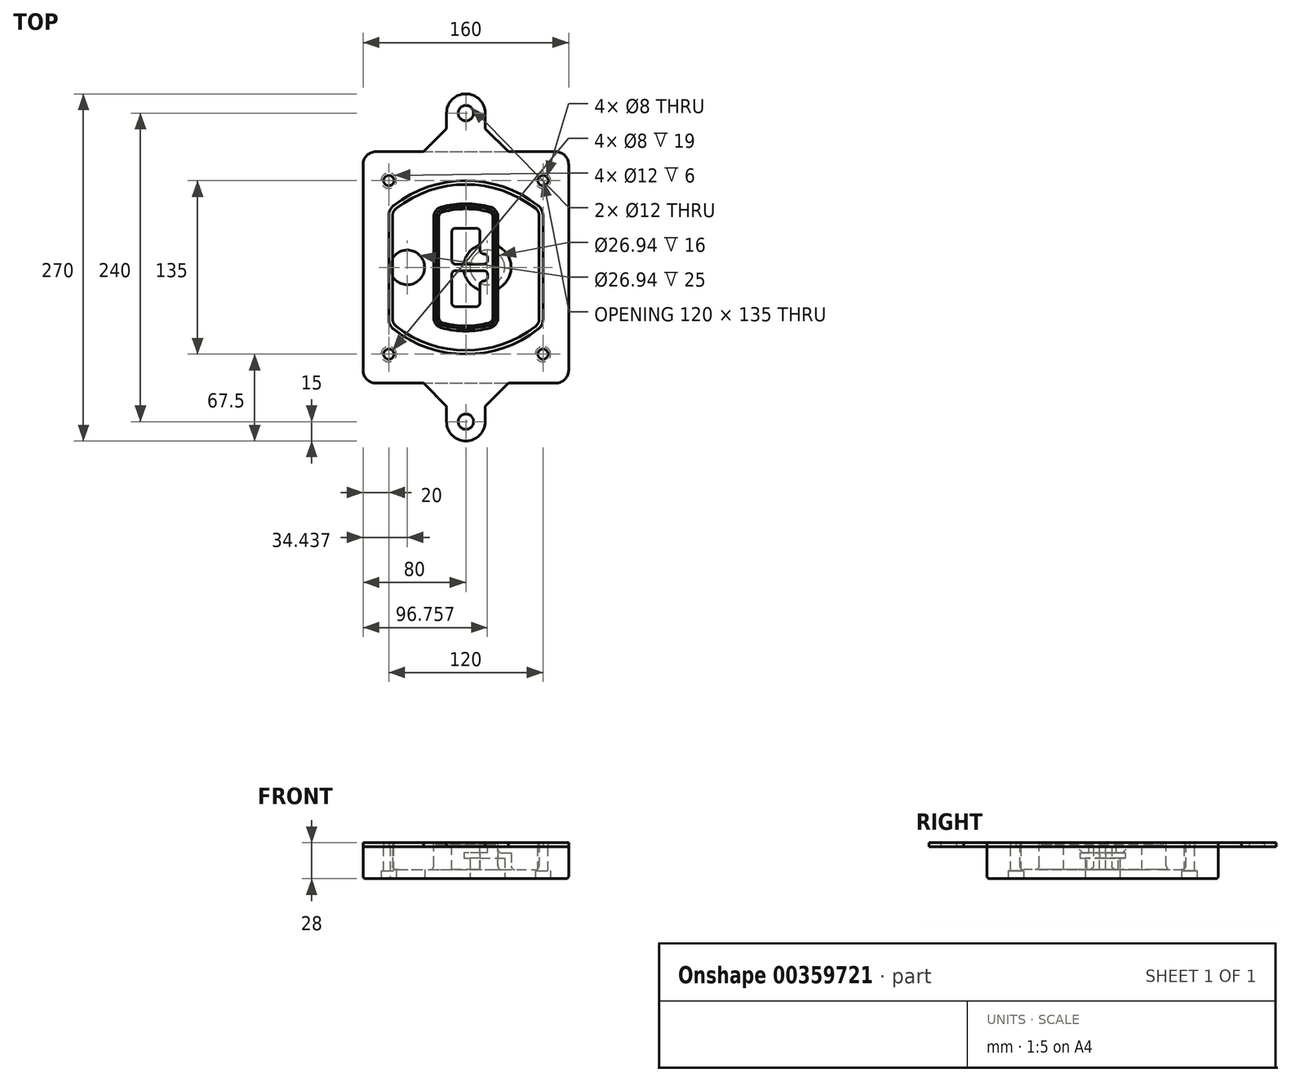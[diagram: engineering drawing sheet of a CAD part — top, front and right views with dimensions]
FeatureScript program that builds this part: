
annotation { "Feature Type Name" : "Feature", "Feature Type Description" : "" }
export const myFeature = defineFeature(function(context is Context, id is Id, definition is map)
    precondition{}
    {
        {
            var Q0;
            Q0=qCreatedBy(makeId("Top.planeOp"),FACE);
            var sketch = newSketch(context, id + "F0", { "sketchPlane" : qUnion([Q0])});
            skPoint(sketch, "E0.rect.middle", {"position": v(0, 0) * mm});
            skLineSegment(sketch, "E1.bottom", {"start": v(-70, -90) * mm, "end": v(70, -90) * mm});
            skLineSegment(sketch, "E1.top", {"start": v(-70, 90) * mm, "end": v(70, 90) * mm});
            skLineSegment(sketch, "E1.left", {"start": v(-80, -80) * mm, "end": v(-80, 80) * mm});
            skLineSegment(sketch, "E1.right", {"start": v(80, -80) * mm, "end": v(80, 80) * mm});
            skLineSegment(sketch, "E2", {"start": v(-80, 90) * mm, "end": v(80, -90) * mm, "construction": true});
            skLineSegment(sketch, "E3", {"start": v(80, 90) * mm, "end": v(-80, -90) * mm, "construction": true});
            skCircle(sketch, "E4", {"center": v(-60, 67.5) * mm, "radius": 4 * mm});
            skCircle(sketch, "E5", {"center": v(60, 67.5) * mm, "radius": 4 * mm});
            skCircle(sketch, "E6", {"center": v(60, -67.5) * mm, "radius": 4 * mm});
            skCircle(sketch, "E7", {"center": v(-60, -67.5) * mm, "radius": 4 * mm});
            skLineSegment(sketch, "E8", {"start": v(-60, 67.5) * mm, "end": v(60, 67.5) * mm, "construction": true});
            skLineSegment(sketch, "E9", {"start": v(60, 67.5) * mm, "end": v(60, -67.5) * mm, "construction": true});
            skLineSegment(sketch, "E10", {"start": v(60, -67.5) * mm, "end": v(-60, -67.5) * mm, "construction": true});
            skLineSegment(sketch, "E11", {"start": v(-60, -67.5) * mm, "end": v(-60, 67.5) * mm, "construction": true});
            skLineSegment(sketch, "E12", {"start": v(-60, 40.3) * mm, "end": v(-60, -40.3) * mm});
            skLineSegment(sketch, "E13", {"start": v(60, 40.3) * mm, "end": v(60, -40.3) * mm});
            skArc(sketch, "E14", {"start": v(56.15, 48.18) * mm, "mid": v(0, 67.5) * mm, "end": v(-56.15, 48.18) * mm});
            skArc(sketch, "E15", {"start": v(-56.15, -48.18) * mm, "mid": v(0, -67.5) * mm, "end": v(56.15, -48.18) * mm});
            skLineSegment(sketch, "E16", {"start": v(-60, 0) * mm, "end": v(60, 0) * mm, "construction": true});
            skPoint(sketch, "E17.visualSharp", {"position": v(-60, -45) * mm});
            skArc(sketch, "E17.filletArc", {"start": v(-60, -40.3) * mm, "mid": v(-58.99, -44.68) * mm, "end": v(-56.15, -48.18) * mm});
            skPoint(sketch, "E18.visualSharp", {"position": v(-60, 45) * mm});
            skArc(sketch, "E18.filletArc", {"start": v(-56.15, 48.18) * mm, "mid": v(-58.99, 44.68) * mm, "end": v(-60, 40.3) * mm});
            skPoint(sketch, "E19.visualSharp", {"position": v(60, 45) * mm});
            skArc(sketch, "E19.filletArc", {"start": v(60, 40.3) * mm, "mid": v(58.99, 44.68) * mm, "end": v(56.15, 48.18) * mm});
            skPoint(sketch, "E20.visualSharp", {"position": v(60, -45) * mm});
            skArc(sketch, "E20.filletArc", {"start": v(56.15, -48.18) * mm, "mid": v(58.99, -44.68) * mm, "end": v(60, -40.3) * mm});
            skPoint(sketch, "E21.visualSharp", {"position": v(-80, 90) * mm});
            skArc(sketch, "E21.filletArc", {"start": v(-70, 90) * mm, "mid": v(-77.07, 87.07) * mm, "end": v(-80, 80) * mm});
            skPoint(sketch, "E22.visualSharp", {"position": v(80, 90) * mm});
            skArc(sketch, "E22.filletArc", {"start": v(80, 80) * mm, "mid": v(77.07, 87.07) * mm, "end": v(70, 90) * mm});
            skPoint(sketch, "E23.visualSharp", {"position": v(80, -90) * mm});
            skArc(sketch, "E23.filletArc", {"start": v(70, -90) * mm, "mid": v(77.07, -87.07) * mm, "end": v(80, -80) * mm});
            skPoint(sketch, "E24.visualSharp", {"position": v(-80, -90) * mm});
            skArc(sketch, "E24.filletArc", {"start": v(-80, -80) * mm, "mid": v(-77.07, -87.07) * mm, "end": v(-70, -90) * mm});
            skArc(sketch, "E25.0", {"start": v(57, 40.3) * mm, "mid": v(56.3, 43.36) * mm, "end": v(54.3, 45.81) * mm});
            skLineSegment(sketch, "E25.1", {"start": v(57, 40.3) * mm, "end": v(57, -40.3) * mm});
            skArc(sketch, "E25.2", {"start": v(54.3, -45.81) * mm, "mid": v(56.3, -43.36) * mm, "end": v(57, -40.3) * mm});
            skArc(sketch, "E25.3", {"start": v(-54.3, -45.81) * mm, "mid": v(0, -64.5) * mm, "end": v(54.3, -45.81) * mm});
            skArc(sketch, "E25.4", {"start": v(-57, -40.3) * mm, "mid": v(-56.3, -43.36) * mm, "end": v(-54.3, -45.81) * mm});
            skArc(sketch, "E25.5", {"start": v(54.3, 45.81) * mm, "mid": v(0, 64.5) * mm, "end": v(-54.3, 45.81) * mm});
            skLineSegment(sketch, "E25.6", {"start": v(-57, 40.3) * mm, "end": v(-57, -40.3) * mm});
            skArc(sketch, "E25.7", {"start": v(-54.3, 45.81) * mm, "mid": v(-56.3, 43.36) * mm, "end": v(-57, 40.3) * mm});
            skArc(sketch, "E26.0", {"start": v(-58.62, 51.33) * mm, "mid": v(-62.58, 46.43) * mm, "end": v(-64, 40.3) * mm});
            skArc(sketch, "E26.1", {"start": v(58.62, 51.33) * mm, "mid": v(0, 71.5) * mm, "end": v(-58.62, 51.33) * mm});
            skArc(sketch, "E26.2", {"start": v(64, 40.3) * mm, "mid": v(62.58, 46.43) * mm, "end": v(58.62, 51.33) * mm});
            skLineSegment(sketch, "E26.3", {"start": v(64, 40.3) * mm, "end": v(64, -40.3) * mm});
            skArc(sketch, "E26.4", {"start": v(58.62, -51.33) * mm, "mid": v(62.58, -46.43) * mm, "end": v(64, -40.3) * mm});
            skLineSegment(sketch, "E26.5", {"start": v(-64, 40.3) * mm, "end": v(-64, -40.3) * mm});
            skArc(sketch, "E26.6", {"start": v(-58.62, -51.33) * mm, "mid": v(0, -71.5) * mm, "end": v(58.62, -51.33) * mm});
            skArc(sketch, "E26.7", {"start": v(-64, -40.3) * mm, "mid": v(-62.58, -46.43) * mm, "end": v(-58.62, -51.33) * mm});
            skSolve(sketch);
        }
        {
            var Q0;
            Q0=makeQuery(id+"F0.imprint","IMPRINT",FACE,{"disambiguationData":[TD([[makeQuery(id+"F0.imprint","IMPRINT",EDGE,{"derivedFrom":sQuery(id+"F0.wireOp",EDGE,"E1.bottom")}),1.0]])]});
            var Q1;
            Q1=makeQuery(id+"F0.imprint","IMPRINT",FACE,{"disambiguationData":[TD([[makeQuery(id+"F0.imprint","IMPRINT",EDGE,{"derivedFrom":sQuery(id+"F0.wireOp",EDGE,"E12")}),1.0]])]});
            var Q2;
            Q2=makeQuery(id+"F0.imprint","IMPRINT",FACE,{"disambiguationData":[TD([[makeQuery(id+"F0.imprint","IMPRINT",EDGE,{"derivedFrom":sQuery(id+"F0.wireOp",EDGE,"E25.0")}),1.0]])]});
            var Q3;
            Q3=makeQuery(id+"F0.imprint","IMPRINT",FACE,{"disambiguationData":[TD([[makeQuery(id+"F0.imprint","IMPRINT",EDGE,{"derivedFrom":sQuery(id+"F0.wireOp",EDGE,"E12")}),-1.0]])]});
            extrude(context, id + "F1", {"entities" : qUnion([Q0, Q1, Q2, Q3]), "oppositeDirection" : true, "depth" : 25 * mm});
        }
        {
            var Q0;
            Q0=makeQuery(id+"F0.imprint","IMPRINT",FACE,{"disambiguationData":[TD([[makeQuery(id+"F0.imprint","IMPRINT",EDGE,{"derivedFrom":sQuery(id+"F0.wireOp",EDGE,"E12")}),1.0]])]});
            extrude(context, id + "F2", {"entities" : qUnion([Q0]), "operationType" : NewBodyOperationType.ADD, "depth" : 3 * mm});
        }
        {
            var Q0;
            Q0=makeQuery(id+"F0.imprint","IMPRINT",FACE,{"disambiguationData":[TD([[makeQuery(id+"F0.imprint","IMPRINT",EDGE,{"derivedFrom":sQuery(id+"F0.wireOp",EDGE,"E25.0")}),1.0]])]});
            extrude(context, id + "F3", {"entities" : qUnion([Q0]), "operationType" : NewBodyOperationType.REMOVE, "oppositeDirection" : true, "depth" : 18 * mm});
        }
        {
            var Q0;
            Q0=makeQuery(id+"F2.opExtrude","CAP_FACE",FACE,{"disambiguationData":[OSD([sQuery(id+"F0.wireOp",EDGE,"E12"),sQuery(id+"F0.wireOp",EDGE,"E13"),sQuery(id+"F0.wireOp",EDGE,"E14"),sQuery(id+"F0.wireOp",EDGE,"E15"),sQuery(id+"F0.wireOp",EDGE,"E17.filletArc"),sQuery(id+"F0.wireOp",EDGE,"E18.filletArc"),sQuery(id+"F0.wireOp",EDGE,"E19.filletArc"),sQuery(id+"F0.wireOp",EDGE,"E20.filletArc"),sQuery(id+"F0.wireOp",EDGE,"E25.0"),sQuery(id+"F0.wireOp",EDGE,"E25.1"),sQuery(id+"F0.wireOp",EDGE,"E25.2"),sQuery(id+"F0.wireOp",EDGE,"E25.3"),sQuery(id+"F0.wireOp",EDGE,"E25.4"),sQuery(id+"F0.wireOp",EDGE,"E25.5"),sQuery(id+"F0.wireOp",EDGE,"E25.6"),sQuery(id+"F0.wireOp",EDGE,"E25.7")])],"isStart":false});
            var sketch = newSketch(context, id + "F4", { "sketchPlane" : qUnion([Q0])});
            skArc(sketch, "E27.0", {"start": v(-19.08, -46.97) * mm, "mid": v(0, -49.5) * mm, "end": v(19.08, -46.97) * mm});
            skArc(sketch, "E28.0", {"start": v(19.08, 46.97) * mm, "mid": v(0, 49.5) * mm, "end": v(-19.08, 46.97) * mm});
            skLineSegment(sketch, "E29", {"start": v(-25, 39.25) * mm, "end": v(-25, -39.25) * mm});
            skLineSegment(sketch, "E30", {"start": v(25, 39.25) * mm, "end": v(25, -39.25) * mm});
            skLineSegment(sketch, "E31", {"start": v(-25, 45.1) * mm, "end": v(25, 45.1) * mm, "construction": true});
            skLineSegment(sketch, "E32", {"start": v(-25, -45.1) * mm, "end": v(25, -45.1) * mm, "construction": true});
            skPoint(sketch, "E33.visualSharp", {"position": v(-25, 45.1) * mm});
            skArc(sketch, "E33.filletArc", {"start": v(-19.08, 46.97) * mm, "mid": v(-23.35, 44.11) * mm, "end": v(-25, 39.25) * mm});
            skPoint(sketch, "E34.visualSharp", {"position": v(25, 45.1) * mm});
            skArc(sketch, "E34.filletArc", {"start": v(25, 39.25) * mm, "mid": v(23.35, 44.11) * mm, "end": v(19.08, 46.97) * mm});
            skPoint(sketch, "E35.visualSharp", {"position": v(25, -45.1) * mm});
            skArc(sketch, "E35.filletArc", {"start": v(19.08, -46.97) * mm, "mid": v(23.35, -44.11) * mm, "end": v(25, -39.25) * mm});
            skPoint(sketch, "E36.visualSharp", {"position": v(-25, -45.1) * mm});
            skArc(sketch, "E36.filletArc", {"start": v(-25, -39.25) * mm, "mid": v(-23.35, -44.11) * mm, "end": v(-19.08, -46.97) * mm});
            skArc(sketch, "E37.0", {"start": v(54.3, 45.81) * mm, "mid": v(0, 64.5) * mm, "end": v(-54.3, 45.81) * mm});
            skArc(sketch, "E37.1", {"start": v(-54.3, 45.81) * mm, "mid": v(-56.3, 43.36) * mm, "end": v(-57, 40.3) * mm});
            skLineSegment(sketch, "E37.2", {"start": v(-57, 40.3) * mm, "end": v(-57, -40.3) * mm});
            skArc(sketch, "E37.3", {"start": v(-57, -40.3) * mm, "mid": v(-56.3, -43.36) * mm, "end": v(-54.3, -45.81) * mm});
            skArc(sketch, "E37.4", {"start": v(-54.3, -45.81) * mm, "mid": v(0, -64.5) * mm, "end": v(54.3, -45.81) * mm});
            skArc(sketch, "E37.5", {"start": v(54.3, -45.81) * mm, "mid": v(56.3, -43.36) * mm, "end": v(57, -40.3) * mm});
            skLineSegment(sketch, "E37.6", {"start": v(57, 40.3) * mm, "end": v(57, -40.3) * mm});
            skArc(sketch, "E37.7", {"start": v(57, 40.3) * mm, "mid": v(56.3, 43.36) * mm, "end": v(54.3, 45.81) * mm});
            skLineSegment(sketch, "E38.0", {"start": v(23, 39.25) * mm, "end": v(23, -39.25) * mm});
            skArc(sketch, "E38.1", {"start": v(18.56, -45.04) * mm, "mid": v(21.76, -42.9) * mm, "end": v(23, -39.25) * mm});
            skArc(sketch, "E38.2", {"start": v(-18.56, -45.04) * mm, "mid": v(0, -47.5) * mm, "end": v(18.56, -45.04) * mm});
            skArc(sketch, "E38.3", {"start": v(-23, -39.25) * mm, "mid": v(-21.76, -42.9) * mm, "end": v(-18.56, -45.04) * mm});
            skLineSegment(sketch, "E38.4", {"start": v(-23, 39.25) * mm, "end": v(-23, -39.25) * mm});
            skArc(sketch, "E38.5", {"start": v(23, 39.25) * mm, "mid": v(21.76, 42.9) * mm, "end": v(18.56, 45.04) * mm});
            skArc(sketch, "E38.6", {"start": v(-18.56, 45.04) * mm, "mid": v(-21.76, 42.9) * mm, "end": v(-23, 39.25) * mm});
            skArc(sketch, "E38.7", {"start": v(18.56, 45.04) * mm, "mid": v(0, 47.5) * mm, "end": v(-18.56, 45.04) * mm});
            skArc(sketch, "E39.0", {"start": v(21, 39.25) * mm, "mid": v(20.18, 41.68) * mm, "end": v(18.04, 43.1) * mm});
            skLineSegment(sketch, "E39.1", {"start": v(21, 39.25) * mm, "end": v(21, -39.25) * mm});
            skArc(sketch, "E39.2", {"start": v(18.04, -43.1) * mm, "mid": v(20.18, -41.68) * mm, "end": v(21, -39.25) * mm});
            skArc(sketch, "E39.3", {"start": v(-18.04, -43.1) * mm, "mid": v(0, -45.5) * mm, "end": v(18.04, -43.1) * mm});
            skArc(sketch, "E39.4", {"start": v(-21, -39.25) * mm, "mid": v(-20.18, -41.68) * mm, "end": v(-18.04, -43.1) * mm});
            skArc(sketch, "E39.5", {"start": v(18.04, 43.1) * mm, "mid": v(0, 45.5) * mm, "end": v(-18.04, 43.1) * mm});
            skLineSegment(sketch, "E39.6", {"start": v(-21, 39.25) * mm, "end": v(-21, -39.25) * mm});
            skArc(sketch, "E39.7", {"start": v(-18.04, 43.1) * mm, "mid": v(-20.18, 41.68) * mm, "end": v(-21, 39.25) * mm});
            skLineSegment(sketch, "E40", {"start": v(-25, 0) * mm, "end": v(25, 0) * mm, "construction": true});
            skLineSegment(sketch, "E41", {"start": v(-11, 5.5) * mm, "end": v(-11, 27.5) * mm});
            skLineSegment(sketch, "E42", {"start": v(-8, 30.5) * mm, "end": v(8, 30.5) * mm});
            skLineSegment(sketch, "E43", {"start": v(11, 27.5) * mm, "end": v(11, 13.5) * mm});
            skLineSegment(sketch, "E44", {"start": v(14, 10.5) * mm, "end": v(14, 10.5) * mm});
            skLineSegment(sketch, "E45", {"start": v(17, 7.5) * mm, "end": v(17, 5.5) * mm});
            skLineSegment(sketch, "E46", {"start": v(14, 2.5) * mm, "end": v(-8, 2.5) * mm});
            skPoint(sketch, "E47.visualSharp", {"position": v(-11, 30.5) * mm});
            skArc(sketch, "E47.filletArc", {"start": v(-8, 30.5) * mm, "mid": v(-10.12, 29.62) * mm, "end": v(-11, 27.5) * mm});
            skPoint(sketch, "E48.visualSharp", {"position": v(11, 30.5) * mm});
            skArc(sketch, "E48.filletArc", {"start": v(11, 27.5) * mm, "mid": v(10.12, 29.62) * mm, "end": v(8, 30.5) * mm});
            skPoint(sketch, "E49.visualSharp", {"position": v(11, 10.5) * mm});
            skArc(sketch, "E49.filletArc", {"start": v(11, 13.5) * mm, "mid": v(11.88, 11.38) * mm, "end": v(14, 10.5) * mm});
            skPoint(sketch, "E50.visualSharp", {"position": v(17, 10.5) * mm});
            skArc(sketch, "E50.filletArc", {"start": v(17, 7.5) * mm, "mid": v(16.12, 9.62) * mm, "end": v(14, 10.5) * mm});
            skPoint(sketch, "E51.visualSharp", {"position": v(17, 2.5) * mm});
            skArc(sketch, "E51.filletArc", {"start": v(14, 2.5) * mm, "mid": v(16.12, 3.38) * mm, "end": v(17, 5.5) * mm});
            skPoint(sketch, "E52.visualSharp", {"position": v(-11, 2.5) * mm});
            skArc(sketch, "E52.filletArc", {"start": v(-11, 5.5) * mm, "mid": v(-10.12, 3.38) * mm, "end": v(-8, 2.5) * mm});
            skLineSegment(sketch, "E53.0.MirrorCS", {"start": v(14, -2.5) * mm, "end": v(-8, -2.5) * mm});
            skArc(sketch, "E54.0.MirrorCS", {"start": v(-11, -5.5) * mm, "mid": v(-10.12, -3.38) * mm, "end": v(-8, -2.5) * mm});
            skLineSegment(sketch, "E55.0.MirrorCS", {"start": v(-11, -5.5) * mm, "end": v(-11, -27.5) * mm});
            skArc(sketch, "E56.0.MirrorCS", {"start": v(-8, -30.5) * mm, "mid": v(-10.12, -29.62) * mm, "end": v(-11, -27.5) * mm});
            skLineSegment(sketch, "E57.0.MirrorCS", {"start": v(-8, -30.5) * mm, "end": v(8, -30.5) * mm});
            skArc(sketch, "E58.0.MirrorCS", {"start": v(11, -27.5) * mm, "mid": v(10.12, -29.62) * mm, "end": v(8, -30.5) * mm});
            skLineSegment(sketch, "E59.0.MirrorCS", {"start": v(11, -27.5) * mm, "end": v(11, -13.5) * mm});
            skArc(sketch, "E60.0.MirrorCS", {"start": v(11, -13.5) * mm, "mid": v(11.88, -11.38) * mm, "end": v(14, -10.5) * mm});
            skArc(sketch, "E61.0.MirrorCS", {"start": v(17, -7.5) * mm, "mid": v(16.12, -9.62) * mm, "end": v(14, -10.5) * mm});
            skLineSegment(sketch, "E62.0.MirrorCS", {"start": v(17, -7.5) * mm, "end": v(17, -5.5) * mm});
            skArc(sketch, "E63.0.MirrorCS", {"start": v(14, -2.5) * mm, "mid": v(16.12, -3.38) * mm, "end": v(17, -5.5) * mm});
            skSolve(sketch);
        }
        {
            var Q0;
            Q0=makeQuery(id+"F4.imprint","IMPRINT",FACE,{"disambiguationData":[TD([[makeQuery(id+"F4.imprint","IMPRINT",EDGE,{"derivedFrom":sQuery(id+"F4.wireOp",EDGE,"E27.0")}),1.0]])]});
            var Q1;
            Q1=makeQuery(id+"F4.imprint","IMPRINT",FACE,{"disambiguationData":[TD([[makeQuery(id+"F4.imprint","IMPRINT",EDGE,{"derivedFrom":sQuery(id+"F4.wireOp",EDGE,"E38.0")}),-1.0]])]});
            var Q2;
            Q2=makeQuery(id+"F4.imprint","IMPRINT",FACE,{"disambiguationData":[TD([[makeQuery(id+"F4.imprint","IMPRINT",EDGE,{"derivedFrom":sQuery(id+"F4.wireOp",EDGE,"E39.0")}),1.0]])]});
            extrude(context, id + "F5", {"entities" : qUnion([Q0, Q1, Q2]), "operationType" : NewBodyOperationType.ADD, "endBound" : BoundingType.UP_TO_NEXT, "oppositeDirection" : true, "depth" : 25 * mm});
        }
        {
            var Q0;
            Q0=makeQuery(id+"F4.imprint","IMPRINT",FACE,{"disambiguationData":[TD([[makeQuery(id+"F4.imprint","IMPRINT",EDGE,{"derivedFrom":sQuery(id+"F4.wireOp",EDGE,"E38.0")}),-1.0]])]});
            extrude(context, id + "F6", {"entities" : qUnion([Q0]), "operationType" : NewBodyOperationType.REMOVE, "oppositeDirection" : true, "depth" : 2 * mm});
        }
        {
            var Q0;
            Q0=makeQuery(id+"F1.opExtrude","CAP_FACE",FACE,{"disambiguationData":[OSD([sQuery(id+"F0.wireOp",EDGE,"E1.bottom"),sQuery(id+"F0.wireOp",EDGE,"E1.top"),sQuery(id+"F0.wireOp",EDGE,"E1.left"),sQuery(id+"F0.wireOp",EDGE,"E1.right"),sQuery(id+"F0.wireOp",EDGE,"E4"),sQuery(id+"F0.wireOp",EDGE,"E5"),sQuery(id+"F0.wireOp",EDGE,"E6"),sQuery(id+"F0.wireOp",EDGE,"E7"),sQuery(id+"F0.wireOp",EDGE,"E21.filletArc"),sQuery(id+"F0.wireOp",EDGE,"E22.filletArc"),sQuery(id+"F0.wireOp",EDGE,"E23.filletArc"),sQuery(id+"F0.wireOp",EDGE,"E24.filletArc")])],"isStart":false});
            var sketch = newSketch(context, id + "F7", { "sketchPlane" : qUnion([Q0])});
            skCircle(sketch, "E64", {"center": v(16.76, 0) * mm, "radius": 13.47 * mm});
            skCircle(sketch, "E65", {"center": v(-45.56, 0) * mm, "radius": 13.47 * mm});
            skLineSegment(sketch, "E66", {"start": v(80, 0) * mm, "end": v(-80, 0) * mm});
            skCircle(sketch, "E67", {"center": v(16.76, 0) * mm, "radius": 18.47 * mm});
            skCircle(sketch, "E68", {"center": v(60, -67.5) * mm, "radius": 6 * mm});
            skCircle(sketch, "E69", {"center": v(-60, -67.5) * mm, "radius": 6 * mm});
            skCircle(sketch, "E70", {"center": v(-60, 67.5) * mm, "radius": 6 * mm});
            skCircle(sketch, "E71", {"center": v(60, 67.5) * mm, "radius": 6 * mm});
            skSolve(sketch);
        }
        {
            var Q0;
            {var subQ1=sQuery(id+"F7.wireOp",EDGE,"E66");var subQ4=sQuery(id+"F7.wireOp",EDGE,"E64");var subQ6=makeQuery(id+"F7.imprint","INTERSECT",VERTEX,{"disambiguationData":[OD(0.0)],"derivedFrom":[subQ4,subQ1]});Q0=makeQuery(id+"F7.imprint","IMPRINT",FACE,{"disambiguationData":[TD([[makeQuery(id+"F7.imprint","IMPRINT",EDGE,{"disambiguationData":[TD([[subQ6,-1.0]])],"derivedFrom":subQ4}),-1.0]])]});}
            var Q1;
            {var subQ0=sQuery(id+"F7.wireOp",EDGE,"E66");var subQ1=sQuery(id+"F7.wireOp",EDGE,"E64");var subQ3=makeQuery(id+"F7.imprint","INTERSECT",VERTEX,{"disambiguationData":[OD(0.0)],"derivedFrom":[subQ1,subQ0]});Q1=makeQuery(id+"F7.imprint","IMPRINT",FACE,{"disambiguationData":[TD([[makeQuery(id+"F7.imprint","IMPRINT",EDGE,{"disambiguationData":[TD([[subQ3,-1.0]])],"derivedFrom":subQ1}),1.0]])]});}
            var Q2;
            {var subQ0=sQuery(id+"F7.wireOp",EDGE,"E66");var subQ1=sQuery(id+"F7.wireOp",EDGE,"E64");var subQ3=makeQuery(id+"F7.imprint","INTERSECT",VERTEX,{"disambiguationData":[OD(0.0)],"derivedFrom":[subQ1,subQ0]});Q2=makeQuery(id+"F7.imprint","IMPRINT",FACE,{"disambiguationData":[TD([[makeQuery(id+"F7.imprint","IMPRINT",EDGE,{"disambiguationData":[TD([[subQ3,1.0]])],"derivedFrom":subQ1}),1.0]])]});}
            var Q3;
            {var subQ1=sQuery(id+"F7.wireOp",EDGE,"E66");var subQ4=sQuery(id+"F7.wireOp",EDGE,"E64");var subQ6=makeQuery(id+"F7.imprint","INTERSECT",VERTEX,{"disambiguationData":[OD(0.0)],"derivedFrom":[subQ4,subQ1]});Q3=makeQuery(id+"F7.imprint","IMPRINT",FACE,{"disambiguationData":[TD([[makeQuery(id+"F7.imprint","IMPRINT",EDGE,{"disambiguationData":[TD([[subQ6,1.0]])],"derivedFrom":subQ4}),-1.0]])]});}
            extrude(context, id + "F8", {"entities" : qUnion([Q0, Q1, Q2, Q3]), "operationType" : NewBodyOperationType.ADD, "oppositeDirection" : true, "depth" : 20 * mm});
        }
        {
            var Q0;
            {var subQ0=sQuery(id+"F7.wireOp",EDGE,"E66");var subQ1=sQuery(id+"F7.wireOp",EDGE,"E64");var subQ3=makeQuery(id+"F7.imprint","INTERSECT",VERTEX,{"disambiguationData":[OD(0.0)],"derivedFrom":[subQ1,subQ0]});Q0=makeQuery(id+"F7.imprint","IMPRINT",FACE,{"disambiguationData":[TD([[makeQuery(id+"F7.imprint","IMPRINT",EDGE,{"disambiguationData":[TD([[subQ3,-1.0]])],"derivedFrom":subQ1}),1.0]])]});}
            var Q1;
            {var subQ0=sQuery(id+"F7.wireOp",EDGE,"E66");var subQ1=sQuery(id+"F7.wireOp",EDGE,"E64");var subQ3=makeQuery(id+"F7.imprint","INTERSECT",VERTEX,{"disambiguationData":[OD(0.0)],"derivedFrom":[subQ1,subQ0]});Q1=makeQuery(id+"F7.imprint","IMPRINT",FACE,{"disambiguationData":[TD([[makeQuery(id+"F7.imprint","IMPRINT",EDGE,{"disambiguationData":[TD([[subQ3,1.0]])],"derivedFrom":subQ1}),1.0]])]});}
            extrude(context, id + "F9", {"entities" : qUnion([Q0, Q1]), "operationType" : NewBodyOperationType.REMOVE, "oppositeDirection" : true, "depth" : 16 * mm});
        }
        {
            var Q0;
            {var subQ0=sQuery(id+"F7.wireOp",EDGE,"E66");var subQ1=sQuery(id+"F7.wireOp",EDGE,"E65");var subQ3=makeQuery(id+"F7.imprint","INTERSECT",VERTEX,{"disambiguationData":[OD(0.0)],"derivedFrom":[subQ1,subQ0]});Q0=makeQuery(id+"F7.imprint","IMPRINT",FACE,{"disambiguationData":[TD([[makeQuery(id+"F7.imprint","IMPRINT",EDGE,{"disambiguationData":[TD([[subQ3,-1.0]])],"derivedFrom":subQ1}),1.0]])]});}
            var Q1;
            {var subQ0=sQuery(id+"F7.wireOp",EDGE,"E66");var subQ1=sQuery(id+"F7.wireOp",EDGE,"E65");var subQ3=makeQuery(id+"F7.imprint","INTERSECT",VERTEX,{"disambiguationData":[OD(0.0)],"derivedFrom":[subQ1,subQ0]});Q1=makeQuery(id+"F7.imprint","IMPRINT",FACE,{"disambiguationData":[TD([[makeQuery(id+"F7.imprint","IMPRINT",EDGE,{"disambiguationData":[TD([[subQ3,1.0]])],"derivedFrom":subQ1}),1.0]])]});}
            extrude(context, id + "F10", {"entities" : qUnion([Q0, Q1]), "operationType" : NewBodyOperationType.REMOVE, "oppositeDirection" : true, "depth" : 25 * mm});
        }
        {
            var Q0;
            Q0=makeQuery(id+"F7.imprint","IMPRINT",FACE,{"disambiguationData":[TD([[makeQuery(id+"F7.imprint","IMPRINT",EDGE,{"derivedFrom":sQuery(id+"F7.wireOp",EDGE,"E68")}),1.0]])]});
            var Q1;
            Q1=makeQuery(id+"F7.imprint","IMPRINT",FACE,{"disambiguationData":[TD([[makeQuery(id+"F7.imprint","IMPRINT",EDGE,{"derivedFrom":makeQuery(id+"F1.opExtrude","CAP_EDGE",EDGE,{"disambiguationData":[OSD([sQuery(id+"F0.wireOp",EDGE,"E5")])],"isStart":false})}),-1.0]])]});
            var Q2;
            Q2=makeQuery(id+"F7.imprint","IMPRINT",FACE,{"disambiguationData":[TD([[makeQuery(id+"F7.imprint","IMPRINT",EDGE,{"derivedFrom":sQuery(id+"F7.wireOp",EDGE,"E69")}),1.0]])]});
            var Q3;
            Q3=makeQuery(id+"F7.imprint","IMPRINT",FACE,{"disambiguationData":[TD([[makeQuery(id+"F7.imprint","IMPRINT",EDGE,{"derivedFrom":makeQuery(id+"F1.opExtrude","CAP_EDGE",EDGE,{"disambiguationData":[OSD([sQuery(id+"F0.wireOp",EDGE,"E4")])],"isStart":false})}),-1.0]])]});
            var Q4;
            Q4=makeQuery(id+"F7.imprint","IMPRINT",FACE,{"disambiguationData":[TD([[makeQuery(id+"F7.imprint","IMPRINT",EDGE,{"derivedFrom":sQuery(id+"F7.wireOp",EDGE,"E70")}),1.0]])]});
            var Q5;
            Q5=makeQuery(id+"F7.imprint","IMPRINT",FACE,{"disambiguationData":[TD([[makeQuery(id+"F7.imprint","IMPRINT",EDGE,{"derivedFrom":makeQuery(id+"F1.opExtrude","CAP_EDGE",EDGE,{"disambiguationData":[OSD([sQuery(id+"F0.wireOp",EDGE,"E7")])],"isStart":false})}),-1.0]])]});
            var Q6;
            Q6=makeQuery(id+"F7.imprint","IMPRINT",FACE,{"disambiguationData":[TD([[makeQuery(id+"F7.imprint","IMPRINT",EDGE,{"derivedFrom":sQuery(id+"F7.wireOp",EDGE,"E71")}),1.0]])]});
            var Q7;
            Q7=makeQuery(id+"F7.imprint","IMPRINT",FACE,{"disambiguationData":[TD([[makeQuery(id+"F7.imprint","IMPRINT",EDGE,{"derivedFrom":makeQuery(id+"F1.opExtrude","CAP_EDGE",EDGE,{"disambiguationData":[OSD([sQuery(id+"F0.wireOp",EDGE,"E6")])],"isStart":false})}),-1.0]])]});
            extrude(context, id + "F11", {"entities" : qUnion([Q0, Q1, Q2, Q3, Q4, Q5, Q6, Q7]), "operationType" : NewBodyOperationType.REMOVE, "oppositeDirection" : true, "depth" : 6 * mm});
        }
        {
            var Q0;
            Q0=makeQuery(id+"F9.boolean.opBoolean","COPY",FACE,{"derivedFrom":makeQuery(id+"F9.opExtrude","CAP_FACE",FACE,{"disambiguationData":[OSD([sQuery(id+"F7.wireOp",EDGE,"E64")])],"isStart":false})});
            var sketch = newSketch(context, id + "F12", { "sketchPlane" : qUnion([Q0])});
            skArc(sketch, "E72.0", {"start": v(11, 17.55) * mm, "mid": v(2.57, 11.82) * mm, "end": v(-1.54, 2.5) * mm});
            skArc(sketch, "E72.1", {"start": v(-1.54, -2.5) * mm, "mid": v(2.57, -11.82) * mm, "end": v(11, -17.55) * mm});
            skLineSegment(sketch, "E73", {"start": v(-1.54, -2.5) * mm, "end": v(14, -2.5) * mm});
            skLineSegment(sketch, "E74.0", {"start": v(14, 2.5) * mm, "end": v(-1.54, 2.5) * mm});
            skArc(sketch, "E74.1", {"start": v(14, 2.5) * mm, "mid": v(16.12, 3.38) * mm, "end": v(17, 5.5) * mm});
            skLineSegment(sketch, "E74.2", {"start": v(17, 7.5) * mm, "end": v(17, 5.5) * mm});
            skArc(sketch, "E74.3", {"start": v(17, 7.5) * mm, "mid": v(16.12, 9.62) * mm, "end": v(14, 10.5) * mm});
            skArc(sketch, "E74.4", {"start": v(11, 13.5) * mm, "mid": v(11.88, 11.38) * mm, "end": v(14, 10.5) * mm});
            skLineSegment(sketch, "E74.5", {"start": v(11, 17.55) * mm, "end": v(11, 13.5) * mm});
            skLineSegment(sketch, "E74.7", {"start": v(14, -2.5) * mm, "end": v(-1.54, -2.5) * mm});
            skArc(sketch, "E74.8", {"start": v(14, -2.5) * mm, "mid": v(16.12, -3.38) * mm, "end": v(17, -5.5) * mm});
            skLineSegment(sketch, "E74.9", {"start": v(17, -7.5) * mm, "end": v(17, -5.5) * mm});
            skArc(sketch, "E74.10", {"start": v(17, -7.5) * mm, "mid": v(16.12, -9.62) * mm, "end": v(14, -10.5) * mm});
            skArc(sketch, "E74.11", {"start": v(11, -13.5) * mm, "mid": v(11.88, -11.38) * mm, "end": v(14, -10.5) * mm});
            skLineSegment(sketch, "E74.12", {"start": v(11, -17.55) * mm, "end": v(11, -13.5) * mm});
            skPoint(sketch, "E75.orphan", {"position": v(11, -27.5) * mm});
            skPoint(sketch, "E76.orphan", {"position": v(-8, -2.5) * mm});
            skPoint(sketch, "E77.orphan", {"position": v(-8, 2.5) * mm});
            skPoint(sketch, "E78.orphan", {"position": v(11, 27.5) * mm});
            skSolve(sketch);
        }
        {
            var Q0;
            {var subQ7=sQuery(id+"F12.wireOp",EDGE,"E72.0");var subQ14=sQuery(id+"F12.wireOp",EDGE,"E72.1");var subQ16=sQuery(id+"F12.wireOp",EDGE,"E74.1");var subQ18=sQuery(id+"F12.wireOp",EDGE,"E74.8");Q0=qUnion([makeQuery(id+"F12.imprint","IMPRINT",FACE,{"disambiguationData":[TD([[makeQuery(id+"F12.imprint","IMPRINT",EDGE,{"derivedFrom":subQ7}),1.0]])]}),makeQuery(id+"F12.imprint","IMPRINT",FACE,{"disambiguationData":[TD([[makeQuery(id+"F12.imprint","IMPRINT",EDGE,{"derivedFrom":subQ14}),1.0]])]}),makeQuery(id+"F12.imprint","IMPRINT",FACE,{"disambiguationData":[TD([[makeQuery(id+"F12.imprint","IMPRINT",EDGE,{"derivedFrom":subQ16}),1.0]])]}),makeQuery(id+"F12.imprint","IMPRINT",FACE,{"disambiguationData":[TD([[makeQuery(id+"F12.imprint","IMPRINT",EDGE,{"derivedFrom":subQ18}),-1.0]])]})]);}
            var Q1;
            Q1=makeQuery(id+"F5.boolean.opBoolean","SPLIT",FACE,{"disambiguationData":[TD([makeQuery(id+"F5.opExtrude","SWEPT_FACE",FACE,{"disambiguationData":[OSD([sQuery(id+"F4.wireOp",EDGE,"E41")])]})])],"derivedFrom":makeQuery(id+"F3.boolean.opBoolean","COPY",FACE,{"derivedFrom":makeQuery(id+"F3.opExtrude","CAP_FACE",FACE,{"disambiguationData":[OSD([sQuery(id+"F0.wireOp",EDGE,"E25.0"),sQuery(id+"F0.wireOp",EDGE,"E25.1"),sQuery(id+"F0.wireOp",EDGE,"E25.2"),sQuery(id+"F0.wireOp",EDGE,"E25.3"),sQuery(id+"F0.wireOp",EDGE,"E25.4"),sQuery(id+"F0.wireOp",EDGE,"E25.5"),sQuery(id+"F0.wireOp",EDGE,"E25.6"),sQuery(id+"F0.wireOp",EDGE,"E25.7")])],"isStart":false})})});
            extrude(context, id + "F13", {"entities" : qUnion([Q0]), "operationType" : NewBodyOperationType.REMOVE, "endBound" : BoundingType.UP_TO_SURFACE, "endBoundEntityFace" : qUnion([Q1]), "depth" : 25 * mm});
        }
        {
            var Q0;
            Q0=makeQuery(id+"F3.boolean.opBoolean","COPY",EDGE,{"derivedFrom":makeQuery(id+"F3.opExtrude","CAP_EDGE",EDGE,{"disambiguationData":[OSD([sQuery(id+"F0.wireOp",EDGE,"E25.6")])],"isStart":false})});
            var Q1;
            Q1=makeQuery(id+"F8.boolean.opBoolean","INTERSECT",EDGE,{"derivedFrom":[makeQuery(id+"F5.opExtrude","SWEPT_FACE",FACE,{"disambiguationData":[OSD([sQuery(id+"F4.wireOp",EDGE,"E30")])]}),makeQuery(id+"F8.opExtrude","CAP_FACE",FACE,{"disambiguationData":[OSD([sQuery(id+"F7.wireOp",EDGE,"E67")])],"isStart":false})]});
            var Q2;
            Q2=makeQuery(id+"F8.boolean.opBoolean","INTERSECT",EDGE,{"disambiguationData":[OD(1.0)],"derivedFrom":[makeQuery(id+"F5.opExtrude","SWEPT_FACE",FACE,{"disambiguationData":[OSD([sQuery(id+"F4.wireOp",EDGE,"E30")])]}),makeQuery(id+"F8.opExtrude","SWEPT_FACE",FACE,{"disambiguationData":[OSD([sQuery(id+"F7.wireOp",EDGE,"E67")])]})]});
            var Q3;
            {var subQ0=sQuery(id+"F4.wireOp",EDGE,"E30");Q3=makeQuery(id+"F8.boolean.opBoolean","SPLIT",EDGE,{"disambiguationData":[TD([makeQuery(id+"F5.opExtrude","SWEPT_FACE",FACE,{"disambiguationData":[OSD([sQuery(id+"F4.wireOp",EDGE,"E35.filletArc")])]})])],"derivedFrom":makeQuery(id+"F5.opExtrude","CAP_EDGE",EDGE,{"disambiguationData":[OSD([subQ0])],"isStart":false})});}
            var Q4;
            {var subQ0=sQuery(id+"F0.wireOp",EDGE,"E25.7");var subQ1=sQuery(id+"F0.wireOp",EDGE,"E25.1");var subQ2=sQuery(id+"F0.wireOp",EDGE,"E25.6");var subQ3=sQuery(id+"F0.wireOp",EDGE,"E25.5");var subQ4=sQuery(id+"F0.wireOp",EDGE,"E25.4");var subQ5=sQuery(id+"F0.wireOp",EDGE,"E25.0");var subQ6=sQuery(id+"F0.wireOp",EDGE,"E25.2");var subQ7=sQuery(id+"F0.wireOp",EDGE,"E25.3");Q4=makeQuery(id+"F8.boolean.opBoolean","INTERSECT",EDGE,{"derivedFrom":[makeQuery(id+"F5.boolean.opBoolean","SPLIT",FACE,{"disambiguationData":[TD([makeQuery(id+"F2.opExtrude","SWEPT_FACE",FACE,{"disambiguationData":[OSD([subQ5])]})])],"derivedFrom":makeQuery(id+"F3.boolean.opBoolean","COPY",FACE,{"derivedFrom":makeQuery(id+"F3.opExtrude","CAP_FACE",FACE,{"disambiguationData":[OSD([subQ5,subQ1,subQ6,subQ7,subQ4,subQ3,subQ2,subQ0])],"isStart":false})})}),makeQuery(id+"F8.opExtrude","SWEPT_FACE",FACE,{"disambiguationData":[OSD([sQuery(id+"F7.wireOp",EDGE,"E67")])]})]});}
            var Q5;
            Q5=makeQuery(id+"F8.boolean.opBoolean","INTERSECT",EDGE,{"disambiguationData":[OD(0.0)],"derivedFrom":[makeQuery(id+"F5.opExtrude","SWEPT_FACE",FACE,{"disambiguationData":[OSD([sQuery(id+"F4.wireOp",EDGE,"E30")])]}),makeQuery(id+"F8.opExtrude","SWEPT_FACE",FACE,{"disambiguationData":[OSD([sQuery(id+"F7.wireOp",EDGE,"E67")])]})]});
            fillet(context, id + "F14", {"entities" : qUnion([Q0, Q1, Q2, Q3, Q4, Q5]), "radius" : 3 * mm, "tangentPropagation" : true, "allowEdgeOverflow" : false});
        }
        {
            var Q0;
            Q0=makeQuery(id+"F1.opExtrude","CAP_EDGE",EDGE,{"disambiguationData":[OSD([sQuery(id+"F0.wireOp",EDGE,"E1.bottom")])],"isStart":false});
            fillet(context, id + "F15", {"entities" : qUnion([Q0]), "radius" : 2 * mm, "tangentPropagation" : true, "allowEdgeOverflow" : false});
        }
        {
            var Q0;
            {var subQ0=sQuery(id+"F0.wireOp",EDGE,"E21.filletArc");var subQ1=sQuery(id+"F0.wireOp",EDGE,"E7");var subQ2=sQuery(id+"F0.wireOp",EDGE,"E6");var subQ3=sQuery(id+"F0.wireOp",EDGE,"E5");var subQ4=sQuery(id+"F0.wireOp",EDGE,"E4");var subQ5=sQuery(id+"F0.wireOp",EDGE,"E22.filletArc");var subQ6=sQuery(id+"F0.wireOp",EDGE,"E1.bottom");var subQ7=sQuery(id+"F0.wireOp",EDGE,"E1.right");var subQ8=sQuery(id+"F0.wireOp",EDGE,"E1.top");var subQ9=sQuery(id+"F0.wireOp",EDGE,"E1.left");var subQ10=sQuery(id+"F0.wireOp",EDGE,"E23.filletArc");var subQ11=sQuery(id+"F0.wireOp",EDGE,"E24.filletArc");Q0=makeQuery(id+"F2.boolean.opBoolean","SPLIT",FACE,{"disambiguationData":[TD([makeQuery(id+"F1.opExtrude","SWEPT_FACE",FACE,{"disambiguationData":[OSD([subQ6])]})])],"derivedFrom":makeQuery(id+"F1.opExtrude","CAP_FACE",FACE,{"disambiguationData":[OSD([subQ6,subQ8,subQ9,subQ7,subQ4,subQ3,subQ2,subQ1,subQ0,subQ5,subQ10,subQ11])],"isStart":true})});}
            var sketch = newSketch(context, id + "F16", { "sketchPlane" : qUnion([Q0])});
            skLineSegment(sketch, "E79", {"start": v(-33, 90) * mm, "end": v(-15, 108) * mm});
            skLineSegment(sketch, "E80", {"start": v(15, 108) * mm, "end": v(33, 90) * mm});
            skLineSegment(sketch, "E81", {"start": v(-15, 108) * mm, "end": v(-15, 120) * mm});
            skLineSegment(sketch, "E82", {"start": v(15, 108) * mm, "end": v(15, 120) * mm});
            skArc(sketch, "E83", {"start": v(15, 120) * mm, "mid": v(0, 135) * mm, "end": v(-15, 120) * mm});
            skCircle(sketch, "E84", {"center": v(0, 120) * mm, "radius": 6 * mm});
            skLineSegment(sketch, "E85", {"start": v(0, 120) * mm, "end": v(0, 90) * mm, "construction": true});
            skLineSegment(sketch, "E86", {"start": v(-80, 0) * mm, "end": v(80, 0) * mm, "construction": true});
            skLineSegment(sketch, "E87.MirrorCS", {"start": v(33, 156) * mm, "end": v(15, 138) * mm});
            skLineSegment(sketch, "E88.MirrorCS", {"start": v(-33, -90) * mm, "end": v(-15, -108) * mm});
            skLineSegment(sketch, "E89.MirrorCS", {"start": v(-15, -108) * mm, "end": v(-15, -120) * mm});
            skArc(sketch, "E90.MirrorCS", {"start": v(15, -120) * mm, "mid": v(0, -135) * mm, "end": v(-15, -120) * mm});
            skLineSegment(sketch, "E91.MirrorCS", {"start": v(0, -120) * mm, "end": v(0, -90) * mm, "construction": true});
            skCircle(sketch, "E92.MirrorC", {"center": v(0, -120) * mm, "radius": 6 * mm});
            skLineSegment(sketch, "E93.MirrorCS", {"start": v(15, -108) * mm, "end": v(15, -120) * mm});
            skLineSegment(sketch, "E94.MirrorCS", {"start": v(15, -108) * mm, "end": v(33, -90) * mm});
            skSolve(sketch);
        }
        {
            var Q0;
            {var subQ0=sQuery(id+"F16.wireOp",EDGE,"E79");Q0=makeQuery(id+"F16.imprint","IMPRINT",FACE,{"disambiguationData":[TD([[makeQuery(id+"F16.imprint","IMPRINT",EDGE,{"derivedFrom":subQ0}),-1.0]])]});}
            var Q1;
            Q1=makeQuery(id+"F16.imprint","IMPRINT",FACE,{"disambiguationData":[TD([[makeQuery(id+"F16.imprint","IMPRINT",EDGE,{"derivedFrom":makeQuery(id+"F1.opExtrude","CAP_EDGE",EDGE,{"disambiguationData":[OSD([sQuery(id+"F0.wireOp",EDGE,"E1.left")])],"isStart":true})}),-1.0]])]});
            var Q2;
            {var subQ0=sQuery(id+"F16.wireOp",EDGE,"E88.MirrorCS");Q2=makeQuery(id+"F16.imprint","IMPRINT",FACE,{"disambiguationData":[TD([[makeQuery(id+"F16.imprint","IMPRINT",EDGE,{"derivedFrom":subQ0}),1.0]])]});}
            var Q3;
            Q3=makeQuery(id+"F2.opExtrude","CAP_FACE",FACE,{"disambiguationData":[OSD([sQuery(id+"F0.wireOp",EDGE,"E12"),sQuery(id+"F0.wireOp",EDGE,"E13"),sQuery(id+"F0.wireOp",EDGE,"E14"),sQuery(id+"F0.wireOp",EDGE,"E15"),sQuery(id+"F0.wireOp",EDGE,"E17.filletArc"),sQuery(id+"F0.wireOp",EDGE,"E18.filletArc"),sQuery(id+"F0.wireOp",EDGE,"E19.filletArc"),sQuery(id+"F0.wireOp",EDGE,"E20.filletArc"),sQuery(id+"F0.wireOp",EDGE,"E25.0"),sQuery(id+"F0.wireOp",EDGE,"E25.1"),sQuery(id+"F0.wireOp",EDGE,"E25.2"),sQuery(id+"F0.wireOp",EDGE,"E25.3"),sQuery(id+"F0.wireOp",EDGE,"E25.4"),sQuery(id+"F0.wireOp",EDGE,"E25.5"),sQuery(id+"F0.wireOp",EDGE,"E25.6"),sQuery(id+"F0.wireOp",EDGE,"E25.7")])],"isStart":false});
            extrude(context, id + "F17", {"entities" : qUnion([Q0, Q1, Q2]), "endBound" : BoundingType.UP_TO_SURFACE, "endBoundEntityFace" : qUnion([Q3]), "depth" : 25 * mm});
        }
    });
